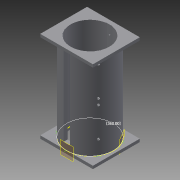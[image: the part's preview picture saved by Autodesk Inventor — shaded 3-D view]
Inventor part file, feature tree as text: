
AUTODESK INVENTOR PART (.ipt)
format: ipt  version: 2013 (Build 170138000, 138)  size: 294,912 bytes
history: native  units: mm
features: sketch x10, extrude x7, other x5, pattern_circular x3, hole x2
ambient origin geometry x8: Origin, YZ Plane, XZ Plane, XY Plane, X Axis, Y Axis, Z Axis, Center Point
feature tree (27):
  other  "ソリッド1"
  extrude  "押し出し1"  Depth=26.0mm
  extrude  "押し出し2"  Depth=20.0mm
  hole  "穴1"  [1 undecoded]
  pattern_circular  "円形状パターン1"  [2 undecoded]
  sketch  "スケッチ4"
  other  "作業平面1"
  other  "作業平面3"
  other  "作業平面7"
  extrude  "押し出し3"  Depth=10.8mm
  pattern_circular  "円形状パターン2"  [2 undecoded]
  other  "作業平面8"
  hole  "穴2"  [1 undecoded]
  pattern_circular  "円形状パターン3"  Count=3 Angle=360.0deg
  extrude  "押し出し4"  Depth=19.5mm
  extrude  "押し出し5"  Depth=4.7mm
  extrude  "押し出し6"  Depth=50.6mm
  extrude  "押し出し7"  Depth=3.0mm
  sketch  "スケッチ1"
  sketch  "スケッチ2"
  sketch  "スケッチ3"
  sketch  "スケッチ5"
  sketch  "スケッチ6"
  sketch  "スケッチ7"
  sketch  "スケッチ8"
  sketch  "スケッチ9"
  sketch  "スケッチ10"
note: 6 required parameter values undecoded (feature->parameter linkage not recoverable at this tier; creation-order binding heuristic only, values carry confidence <= 0.55)
